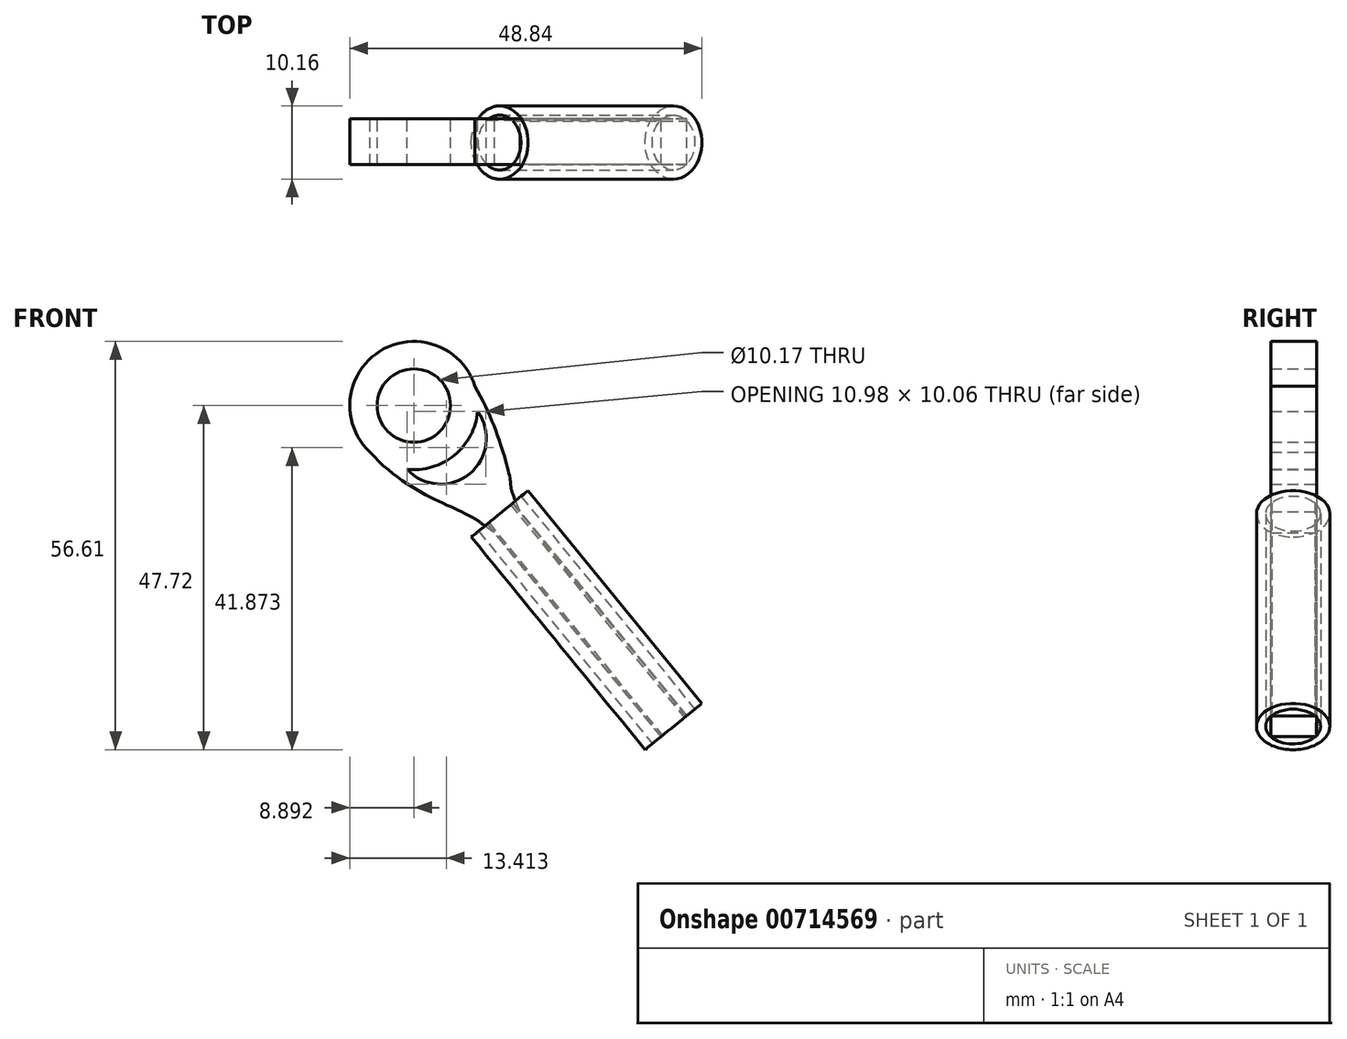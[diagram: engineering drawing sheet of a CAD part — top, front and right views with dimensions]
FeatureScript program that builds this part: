
annotation { "Feature Type Name" : "Feature", "Feature Type Description" : "" }
export const myFeature = defineFeature(function(context is Context, id is Id, definition is map)
    precondition{}
    {
        {
            var Q0;
            Q0=qCreatedBy(makeId("Front.planeOp"),FACE);
            var sketch = newSketch(context, id + "F0", { "sketchPlane" : qUnion([Q0])});
            skCircle(sketch, "E0", {"center": v(35.66, 55.7) * mm, "radius": 88.9 * mm, "construction": true});
            skCircle(sketch, "E1", {"center": v(35.66, 55.7) * mm, "radius": 6.35 * mm});
            skLineSegment(sketch, "E2", {"start": v(35.66, -33.2) * mm, "end": v(-37.46, 5.12) * mm, "construction": true});
            skLineSegment(sketch, "E3", {"start": v(-28.58, -5.76) * mm, "end": v(35.66, -33.2) * mm, "construction": true});
            skLineSegment(sketch, "E4", {"start": v(48.36, 55.57) * mm, "end": v(47.48, -32.41) * mm});
            skLineSegment(sketch, "E5", {"start": v(47.48, -32.41) * mm, "end": v(47.48, -64.2) * mm});
            skLineSegment(sketch, "E6.bottom", {"start": v(-63.98, 6.77) * mm, "end": v(22.98, 55) * mm});
            skLineSegment(sketch, "E6.left", {"start": v(-63.98, 6.77) * mm, "end": v(-46.84, -64.2) * mm});
            skCircle(sketch, "E7", {"center": v(35.66, 55.7) * mm, "radius": 12.7 * mm});
            skCircle(sketch, "E8", {"center": v(35.66, -33.2) * mm, "radius": 6.35 * mm});
            skLineSegment(sketch, "E9", {"start": v(-46.84, -64.2) * mm, "end": v(47.48, -64.2) * mm});
            skLineSegment(sketch, "E10", {"start": v(-37.46, 5.12) * mm, "end": v(-28.58, -5.76) * mm});
            skArc(sketch, "E11.0.startCap", {"start": v(-42.38, 1.1) * mm, "mid": v(-41.47, 10.04) * mm, "end": v(-32.53, 9.14) * mm});
            skArc(sketch, "E11.0.endCap", {"start": v(-23.66, -1.75) * mm, "mid": v(-24.56, -10.68) * mm, "end": v(-33.5, -9.78) * mm});
            skLineSegment(sketch, "E11.0.left", {"start": v(-32.53, 9.14) * mm, "end": v(-23.66, -1.75) * mm});
            skLineSegment(sketch, "E11.0.right", {"start": v(-42.38, 1.1) * mm, "end": v(-33.5, -9.78) * mm});
            skSolve(sketch);
        }
        {
            var Q0;
            {var subQ1=sQuery(id+"F0.wireOp",EDGE,"E4");Q0=makeQuery(id+"F0.imprint","IMPRINT",FACE,{"disambiguationData":[TD([[makeQuery(id+"F0.imprint","IMPRINT",EDGE,{"derivedFrom":subQ1}),-1.0]])]});}
            var sketch = newSketch(context, id + "F1", { "sketchPlane" : qUnion([Q0])});
            skCircle(sketch, "E12", {"center": v(-32.29, -1.22) * mm, "radius": 5.08 * mm});
            skCircle(sketch, "E13", {"center": v(-32.29, -1.22) * mm, "radius": 8.9 * mm});
            skLineSegment(sketch, "E14", {"start": v(-32.29, -1.22) * mm, "end": v(1.1, -42.09) * mm, "construction": true});
            skLineSegment(sketch, "E15.bottom", {"start": v(5.55, -44.23) * mm, "end": v(2, -47.13) * mm});
            skLineSegment(sketch, "E15.top", {"start": v(-17.56, -15.95) * mm, "end": v(-21.1, -18.84) * mm});
            skLineSegment(sketch, "E15.left", {"start": v(5.55, -44.23) * mm, "end": v(-17.56, -15.95) * mm});
            skLineSegment(sketch, "E15.right", {"start": v(2, -47.13) * mm, "end": v(-21.1, -18.84) * mm});
            skFitSpline(sketch, "E16", {"points": [v(-26.61, 5.62) * mm, v(-18.93, -11.55) * mm, v(-17.56, -15.95) * mm], "startDerivative": vector(21.51, -26.6) * mm, "endDerivative": vector(13.85, -30.84) * mm});
            skFitSpline(sketch, "E17", {"points": [v(-38.39, -7.69) * mm, v(-24.83, -16.37) * mm, v(-21.1, -18.84) * mm], "startDerivative": vector(21.43, -23.82) * mm, "endDerivative": vector(11.62, -7.97) * mm});
            skLineSegment(sketch, "E18", {"start": v(-24.83, -16.37) * mm, "end": v(-24.83, -16.37) * mm});
            skLineSegment(sketch, "E19", {"start": v(-18.93, -11.55) * mm, "end": v(-24.83, -16.37) * mm});
            skSolve(sketch);
        }
        {
            var Q0;
            Q0=makeQuery(id+"F1.imprint","IMPRINT",FACE,{"disambiguationData":[TD([[makeQuery(id+"F1.imprint","IMPRINT",EDGE,{"derivedFrom":sQuery(id+"F1.wireOp",EDGE,"E15.bottom")}),-1.0]])]});
            var Q1;
            Q1=makeQuery(id+"F1.imprint","IMPRINT",FACE,{"disambiguationData":[TD([[makeQuery(id+"F1.imprint","IMPRINT",EDGE,{"derivedFrom":sQuery(id+"F1.wireOp",EDGE,"E12")}),-1.0]])]});
            var Q2;
            {var subQ0=sQuery(id+"F1.wireOp",EDGE,"E15.top");Q2=makeQuery(id+"F1.imprint","IMPRINT",FACE,{"disambiguationData":[TD([[makeQuery(id+"F1.imprint","IMPRINT",EDGE,{"derivedFrom":subQ0}),-1.0]])]});}
            var Q3;
            {var subQ0=sQuery(id+"F1.wireOp",EDGE,"E19");Q3=makeQuery(id+"F1.imprint","IMPRINT",FACE,{"disambiguationData":[TD([[makeQuery(id+"F1.imprint","IMPRINT",EDGE,{"derivedFrom":subQ0}),-1.0]])]});}
            var Q4;
            {var subQ4=makeQuery(id+"F0.imprint","IMPRINT",EDGE,{"derivedFrom":sQuery(id+"F0.wireOp",EDGE,"E11.0.left")});Q4=makeQuery(id+"F1.imprint","IMPRINT",FACE,{"disambiguationData":[TD([[makeQuery(id+"F1.imprint","IMPRINT",EDGE,{"derivedFrom":subQ4}),1.0]])]});}
            var Q5;
            {var subQ6=makeQuery(id+"F0.imprint","IMPRINT",EDGE,{"derivedFrom":sQuery(id+"F0.wireOp",EDGE,"E11.0.right")});Q5=makeQuery(id+"F1.imprint","IMPRINT",FACE,{"disambiguationData":[TD([[makeQuery(id+"F1.imprint","IMPRINT",EDGE,{"derivedFrom":subQ6}),-1.0]])]});}
            var Q6;
            {var subQ6=sQuery(id+"F1.wireOp",EDGE,"E16");var subQ7=sQuery(id+"F1.wireOp",EDGE,"E13");var subQ8=makeQuery(id+"F1.imprint","INTERSECT",VERTEX,{"disambiguationData":[OD(1.0)],"derivedFrom":[subQ7,subQ6]});Q6=makeQuery(id+"F1.imprint","IMPRINT",FACE,{"disambiguationData":[TD([[makeQuery(id+"F1.imprint","IMPRINT",EDGE,{"disambiguationData":[TD([[subQ8,-1.0]])],"derivedFrom":subQ7}),1.0]])]});}
            extrude(context, id + "F2", {"entities" : qUnion([Q0, Q1, Q2, Q3, Q4, Q5, Q6]), "depth" : 6.35 * mm, "offsetDistance" : 25.4 * mm});
        }
        {
            var Q0;
            Q0=makeQuery(id+"F2.opExtrude","SWEPT_FACE",FACE,{"disambiguationData":[OSD([sQuery(id+"F1.wireOp",EDGE,"E15.bottom")])]});
            var sketch = newSketch(context, id + "F3", { "sketchPlane" : qUnion([Q0])});
            skCircle(sketch, "E20", {"center": v(-26.05, 3.27) * mm, "radius": 3.81 * mm});
            skCircle(sketch, "E21", {"center": v(-26.05, 3.27) * mm, "radius": 5.08 * mm});
            skSolve(sketch);
        }
        {
            var Q0;
            Q0=makeQuery(id+"F3.imprint","IMPRINT",FACE,{"disambiguationData":[TD([[makeQuery(id+"F3.imprint","IMPRINT",EDGE,{"derivedFrom":sQuery(id+"F3.wireOp",EDGE,"E21")}),1.0]])]});
            extrude(context, id + "F4", {"entities" : qUnion([Q0]), "oppositeDirection" : true, "depth" : 38.1 * mm, "offsetDistance" : 25.4 * mm});
        }
    });
